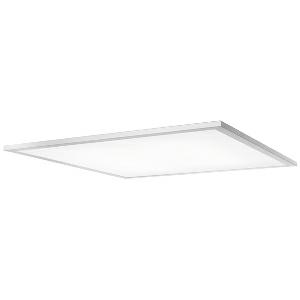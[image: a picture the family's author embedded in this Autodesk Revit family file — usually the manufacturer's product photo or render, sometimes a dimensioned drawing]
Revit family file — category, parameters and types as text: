
# Revit family: dotoo_fit_-_dfe_4000_830_sm625_00808117_af57
name_source: partatom
category: Lighting Fixtures
units: mm (PartAtom-declared; Revit-internal decimal feet)

## family parameters
Cut with Voids When Loaded = No
Host = Face
Light Source = No
Part Type = Normal
Room Calculation Point = No
Round Connector Dimension = Use Diameter
Shared = No

## types (1)
- DOTOO.fit - DFE 4000/830 SM625 (1 x LED, 3900 lm, 4000K)
    Apparent Load = 30 VA
    Approval mark = CE
    CIE Flux Codes = 66 90 98 100 100
    Color Rendering = 80-89
    Color Temperature = 4000K
    Control Gear = Electronic ballast
    Default Elevation = 1800 mm
    Description = DFE 4000/830|Recessed modular luminaire|light source:  |work equipment: Electronic ballast|connected load: 220-240 V, 50/60 Hz|Power consumption: approx. 30 W|standby: approx. 0,50|power factor: approx. 0,900|luminous flux: 3900 lm|luminous efficacy: 130 lm/W|light distribution: Direct|direct ratio: approx. 100 %|colour temperature: Warm white, ca. 3000 K|color rendering index (CRI): >= 80|chromaticity tolerance:  3 SDCM|System of protection: IP 20|class of protection: II|technology: Switchable|operation: External|luminaire body|material: Sectional aluminium|colour: White|weight (net): approx. 3.0 kg|mains lead: 0.50 m Connector|glare control: Prism aperture|luminance(L65): <= 2600 cd/m|unified glare rating(4H 8H): <=  19|special features: Direct light component with edge light and light-guide technology for homogenous light exit, Flicker-free, System dimension 625 x 625 mm, Strain relief with the possibility of through-wiring|
    Height = 0 mm  [stored 0 ft]
    Lamp = 1 x LED
    Lamp Light Flux = 3900 lm
    Lamp count = 1
    Length = 622 mm
    Luminous efficacy = 130 lm/W
    Manufacturer = Waldmann
    ModVariant = No
    Model = 00808117
    Mounting Place = Ceiling
    Mounting Type = Recessed
    Number of Poles = 1
    OnlyDefault = Yes
    Power Factor = 1
    Product Name = DOTOO.fit - DFE 4000/830 SM625
    Product group = Recessed luminaire
    ProductGroupID = 4
    Protection Class = Protection class II
    Protection Degree = IP 20
    RLX_Detail_Level = 1
    RLX_Emergency_Light_Flux = 0 lm
    RLX_Emergency_Type = 0
    RLX_Emergency_Type_DB = No
    RlxData = <blob elided: 37505 chars, md5=d96a3756>
    Socket = socket
    Standby Power = 0 W
    System Light Flux = 3900 lm
    System Power = 30 W
    Type Comments = Product without accessories
    Type Image = 113328000-00692486.jpg
    URL = http://relux.com
    VarID = ---
    Voltage = 230 V
    Voltage Range = 220-240 V
    Weight = 0.00 kg
    Width = 622 mm

note: [stored X ft] marks values corroborated as IEEE doubles in the binary element streams (Revit-internal decimal feet)

## geometry (parser evidence)
native form markers: Blend x4, Sweep x10
no freeform markers — native parametric forms only
